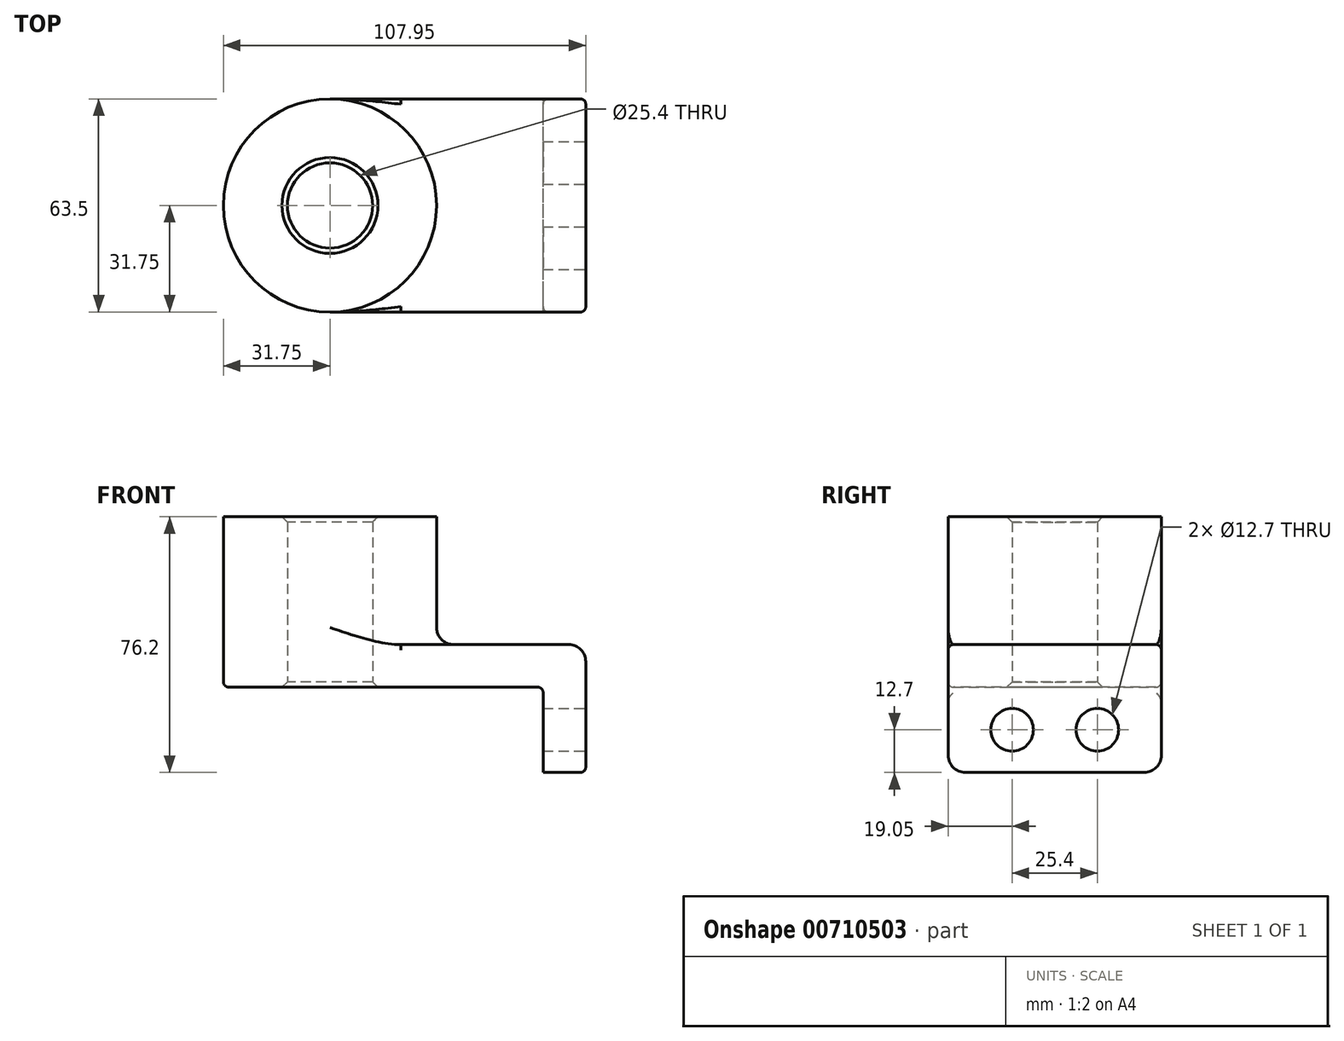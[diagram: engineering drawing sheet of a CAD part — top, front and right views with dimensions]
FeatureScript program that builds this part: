
annotation { "Feature Type Name" : "Feature", "Feature Type Description" : "" }
export const myFeature = defineFeature(function(context is Context, id is Id, definition is map)
    precondition{}
    {
        {
            var Q0;
            Q0=qCreatedBy(makeId("Top.planeOp"),FACE);
            var sketch = newSketch(context, id + "F0", { "sketchPlane" : qUnion([Q0])});
            skLineSegment(sketch, "E0.bottom", {"start": v(38.1, -31.75) * mm, "end": v(-38.1, -31.75) * mm});
            skLineSegment(sketch, "E0.top", {"start": v(38.1, 31.75) * mm, "end": v(-38.1, 31.75) * mm});
            skLineSegment(sketch, "E0.left", {"start": v(38.1, -31.75) * mm, "end": v(38.1, 31.75) * mm});
            skLineSegment(sketch, "E0.right", {"start": v(-38.1, -31.75) * mm, "end": v(-38.1, 31.75) * mm});
            skPoint(sketch, "E0.middle", {"position": v(0, 0) * mm});
            skCircle(sketch, "E1", {"center": v(-38.1, 0) * mm, "radius": 31.75 * mm});
            skCircle(sketch, "E2", {"center": v(-38.1, 0) * mm, "radius": 12.7 * mm});
            skSolve(sketch);
        }
        {
            var Q0;
            Q0 = qSketchRegion(id + "F0", true);
            extrude(context, id + "F1", {"entities" : qUnion([Q0]), "depth" : 12.7 * mm, "offsetDistance" : 25.4 * mm});
        }
        {
            var Q0;
            {var subQ1=sQuery(id+"F0.wireOp",EDGE,"E0.right");var subQ3=sQuery(id+"F0.wireOp",EDGE,"E2");var subQ4=makeQuery(id+"F0.imprint","INTERSECT",VERTEX,{"disambiguationData":[OD(0.0)],"derivedFrom":[subQ1,subQ3]});Q0=makeQuery(id+"F0.imprint","IMPRINT",FACE,{"disambiguationData":[TD([[makeQuery(id+"F0.imprint","IMPRINT",EDGE,{"disambiguationData":[TD([[subQ4,1.0]])],"derivedFrom":subQ3}),-1.0]])]});}
            var Q1;
            {var subQ1=sQuery(id+"F0.wireOp",EDGE,"E0.right");var subQ3=sQuery(id+"F0.wireOp",EDGE,"E2");var subQ4=makeQuery(id+"F0.imprint","INTERSECT",VERTEX,{"disambiguationData":[OD(0.0)],"derivedFrom":[subQ1,subQ3]});Q1=makeQuery(id+"F0.imprint","IMPRINT",FACE,{"disambiguationData":[TD([[makeQuery(id+"F0.imprint","IMPRINT",EDGE,{"disambiguationData":[TD([[subQ4,-1.0]])],"derivedFrom":subQ3}),-1.0]])]});}
            extrude(context, id + "F2", {"entities" : qUnion([Q0, Q1]), "operationType" : NewBodyOperationType.ADD, "depth" : 50.8 * mm, "offsetDistance" : 25.4 * mm});
        }
        {
            var Q0;
            Q0=makeQuery(id+"F1.opExtrude","SWEPT_FACE",FACE,{"disambiguationData":[OSD([sQuery(id+"F0.wireOp",EDGE,"E0.left")])]});
            var sketch = newSketch(context, id + "F3", { "sketchPlane" : qUnion([Q0])});
            skLineSegment(sketch, "E3.bottom", {"start": v(-31.75, 12.7) * mm, "end": v(31.75, 12.7) * mm});
            skLineSegment(sketch, "E3.top", {"start": v(-31.75, -25.4) * mm, "end": v(31.75, -25.4) * mm});
            skLineSegment(sketch, "E3.left", {"start": v(-31.75, 12.7) * mm, "end": v(-31.75, -25.4) * mm});
            skLineSegment(sketch, "E3.right", {"start": v(31.75, 12.7) * mm, "end": v(31.75, -25.4) * mm});
            skCircle(sketch, "E4", {"center": v(-12.7, -12.7) * mm, "radius": 6.35 * mm});
            skLineSegment(sketch, "E5", {"start": v(0, 0) * mm, "end": v(0, -25.4) * mm, "construction": true});
            skCircle(sketch, "E6.MirrorC", {"center": v(12.7, -12.7) * mm, "radius": 6.35 * mm});
            skSolve(sketch);
        }
        {
            var Q0;
            Q0 = qSketchRegion(id + "F3", true);
            extrude(context, id + "F4", {"entities" : qUnion([Q0]), "operationType" : NewBodyOperationType.ADD, "oppositeDirection" : true, "depth" : 12.7 * mm, "offsetDistance" : 25.4 * mm});
        }
        {
            var Q0;
            {var subQ0=sQuery(id+"F0.wireOp",EDGE,"E1");Q0=makeQuery(id+"F2.boolean.opBoolean","INTERSECT",EDGE,{"derivedFrom":[makeQuery(id+"F1.opExtrude","CAP_FACE",FACE,{"disambiguationData":[OSD([sQuery(id+"F0.wireOp",EDGE,"E0.bottom"),sQuery(id+"F0.wireOp",EDGE,"E0.top"),sQuery(id+"F0.wireOp",EDGE,"E0.left"),subQ0,sQuery(id+"F0.wireOp",EDGE,"E2")])],"isStart":false}),makeQuery(id+"F2.opExtrude","SWEPT_FACE",FACE,{"disambiguationData":[OSD([subQ0])]})]});}
            var Q1;
            Q1=makeQuery(id+"F1.opExtrude","CAP_EDGE",EDGE,{"disambiguationData":[OSD([sQuery(id+"F0.wireOp",EDGE,"E0.left")])],"isStart":false});
            var Q2;
            Q2=makeQuery(id+"F4.opExtrude","SWEPT_EDGE",EDGE,{"disambiguationData":[OSD([sQuery(id+"F3.wireOp",EDGE,"E3.top"),sQuery(id+"F3.wireOp",EDGE,"E3.right")])]});
            var Q3;
            Q3=makeQuery(id+"F4.opExtrude","SWEPT_EDGE",EDGE,{"disambiguationData":[OSD([sQuery(id+"F3.wireOp",EDGE,"E3.top"),sQuery(id+"F3.wireOp",EDGE,"E3.left")])]});
            fillet(context, id + "F5", {"entities" : qUnion([Q0, Q1, Q2, Q3]), "radius" : 5.08 * mm, "tangentPropagation" : true, "allowEdgeOverflow" : false});
        }
        {
            var Q0;
            Q0=makeQuery(id+"F1.opExtrude","CAP_EDGE",EDGE,{"disambiguationData":[OSD([sQuery(id+"F0.wireOp",EDGE,"E0.bottom")])],"isStart":true});
            var Q1;
            Q1=makeQuery(id+"F1.opExtrude","CAP_EDGE",EDGE,{"disambiguationData":[OSD([sQuery(id+"F0.wireOp",EDGE,"E0.bottom")])],"isStart":false});
            var Q2;
            Q2=makeQuery(id+"F4.boolean.opBoolean","INTERSECT",EDGE,{"derivedFrom":[makeQuery(id+"F1.opExtrude","CAP_FACE",FACE,{"disambiguationData":[OSD([sQuery(id+"F0.wireOp",EDGE,"E0.bottom"),sQuery(id+"F0.wireOp",EDGE,"E0.top"),sQuery(id+"F0.wireOp",EDGE,"E0.left"),sQuery(id+"F0.wireOp",EDGE,"E1"),sQuery(id+"F0.wireOp",EDGE,"E2")])],"isStart":true}),makeQuery(id+"F4.opExtrude","CAP_FACE",FACE,{"disambiguationData":[OSD([sQuery(id+"F3.wireOp",EDGE,"E3.bottom"),sQuery(id+"F3.wireOp",EDGE,"E3.top"),sQuery(id+"F3.wireOp",EDGE,"E3.left"),sQuery(id+"F3.wireOp",EDGE,"E3.right"),sQuery(id+"F3.wireOp",EDGE,"E4"),sQuery(id+"F3.wireOp",EDGE,"E6.MirrorC")])],"isStart":false})]});
            fillet(context, id + "F6", {"entities" : qUnion([Q0, Q1, Q2]), "radius" : 1.59 * mm, "tangentPropagation" : true, "allowEdgeOverflow" : false});
        }
        {
            var Q0;
            {var subQ0=sQuery(id+"F0.wireOp",EDGE,"E2");Q0=makeQuery(id+"F2.boolean.opBoolean","MERGE",FACE,{"derivedFrom":[makeQuery(id+"F1.opExtrude","SWEPT_FACE",FACE,{"disambiguationData":[OSD([subQ0])]}),makeQuery(id+"F2.opExtrude","SWEPT_FACE",FACE,{"disambiguationData":[OSD([subQ0])]})]});}
            chamfer(context, id + "F7", {"entities" : qUnion([Q0]), "width" : 1.59 * mm, "tangentPropagation" : true});
        }
    });
